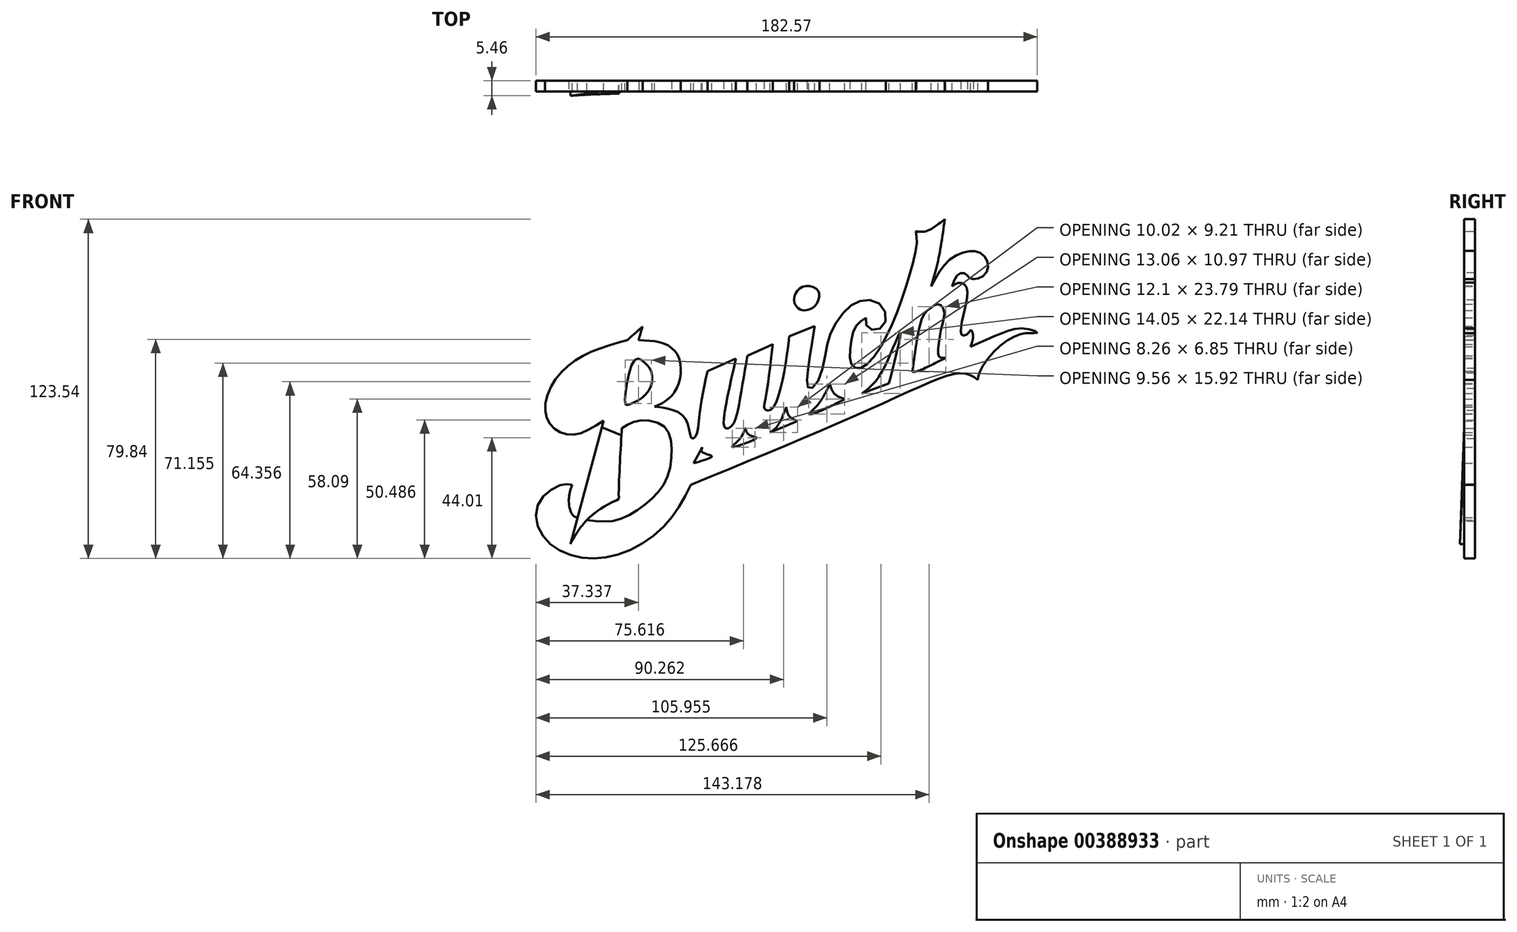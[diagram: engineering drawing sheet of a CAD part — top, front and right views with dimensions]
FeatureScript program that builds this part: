
annotation { "Feature Type Name" : "Feature", "Feature Type Description" : "" }
export const myFeature = defineFeature(function(context is Context, id is Id, definition is map)
    precondition{}
    {
        {
            var Q0;
            Q0=qCreatedBy(makeId("Front.planeOp"),FACE);
            var sketch = newSketch(context, id + "F0", { "sketchPlane" : qUnion([Q0])});
            skFitSpline(sketch, "E0", {"points": [v(-57.53, 21.82) * mm, v(-61.34, 4) * mm, v(-60.54, 3.6) * mm, v(-55.53, 5.8) * mm, v(-50.93, 11.4) * mm, v(-51.13, 17.81) * mm, v(-54.13, 21.22) * mm, v(-57.53, 21.82) * mm]});
            skFitSpline(sketch, "E1", {"points": [v(-62.74, -5.82) * mm, v(-63.94, -33.85) * mm, v(-63.94, -34.65) * mm, v(-65.54, -35.25) * mm, v(-75.96, -42.06) * mm, v(-83.57, -52.67) * mm], "startDerivative": vector(-6.03, -104.62) * mm, "endDerivative": vector(-25.26, -44.77) * mm});
            skFitSpline(sketch, "E2", {"points": [v(-83.57, -52.67) * mm, v(-70.15, -2.81) * mm], "startDerivative": vector(13.42, 49.86) * mm, "endDerivative": vector(13.42, 49.86) * mm});
            skFitSpline(sketch, "E3", {"points": [v(-70.15, -2.81) * mm, v(-81.96, -8.42) * mm, v(-90.17, -5.82) * mm, v(-93.78, 2) * mm, v(-88.97, 14.8) * mm, v(-76.56, 24.42) * mm, v(-60.54, 29.83) * mm], "startDerivative": vector(-70.6, -45.61) * mm, "endDerivative": vector(85.3, 23.4) * mm});
            skFitSpline(sketch, "E4", {"points": [v(-60.54, 29.83) * mm, v(-54.33, 35.23) * mm, v(-53.93, 35.43) * mm], "startDerivative": vector(9.9, 8.94) * mm, "endDerivative": vector(1.6, 0.53) * mm});
            skFitSpline(sketch, "E5", {"points": [v(-54.33, 35.23) * mm, v(-55.86, 29.83) * mm, v(-55.76, 29.83) * mm], "startDerivative": vector(-2.88, -8.83) * mm, "endDerivative": vector(1, 0.36) * mm});
            skFitSpline(sketch, "E6", {"points": [v(-55.76, 29.83) * mm, v(-45.65, 28.41) * mm, v(-39.84, 23.1) * mm, v(-39.44, 13.4) * mm, v(-43.55, 6.39) * mm, v(-49.46, 2.88) * mm], "startDerivative": vector(49.04, -1.87) * mm, "endDerivative": vector(-34.87, -16.17) * mm});
            skFitSpline(sketch, "E7", {"points": [v(-49.46, 2.88) * mm, v(-42.85, 1.78) * mm, v(-36.54, -2.81) * mm, v(-34.54, -9.83) * mm, v(-33.04, -9.43) * mm, v(-31.13, 1.08) * mm, v(-28.13, 17.3) * mm], "startDerivative": vector(41.75, -4.03) * mm, "endDerivative": vector(14.55, 66.04) * mm});
            skFitSpline(sketch, "E8", {"points": [v(-28.13, 17.3) * mm, v(-16.62, 22.3) * mm], "startDerivative": vector(11.51, 5) * mm, "endDerivative": vector(11.51, 5) * mm});
            skFitSpline(sketch, "E9", {"points": [v(-16.62, 22.3) * mm, v(-21.42, -1.72) * mm, v(-20.82, -5.82) * mm, v(-18.12, -4.73) * mm, v(-14.81, 6.89) * mm, v(-11.91, 23.5) * mm], "startDerivative": vector(-21.04, -92.35) * mm, "endDerivative": vector(11.83, 65.59) * mm});
            skFitSpline(sketch, "E10", {"points": [v(-11.91, 23.5) * mm, v(-1.7, 28.11) * mm], "startDerivative": vector(10.21, 4.6) * mm, "endDerivative": vector(10.21, 4.6) * mm});
            skFitSpline(sketch, "E11", {"points": [v(-1.7, 28.11) * mm, v(-4.8, 5.18) * mm, v(-5, 1.98) * mm, v(-2.9, 1.48) * mm, v(1, 8.49) * mm, v(4.4, 26.7) * mm, v(5, 31.32) * mm], "startDerivative": vector(-11.82, -100.44) * mm, "endDerivative": vector(3.65, 29.39) * mm});
            skFitSpline(sketch, "E12", {"points": [v(5, 31.32) * mm, v(15.22, 35.43) * mm], "startDerivative": vector(10.21, 4.12) * mm, "endDerivative": vector(10.21, 4.12) * mm});
            skFitSpline(sketch, "E13", {"points": [v(15.22, 35.43) * mm, v(12.72, 19.1) * mm, v(12.22, 11.8) * mm, v(13.12, 10.19) * mm, v(16.12, 12.5) * mm, v(19.53, 23.5) * mm, v(21.93, 33.02) * mm, v(28.14, 42.23) * mm, v(34.35, 45.83) * mm, v(41.25, 44.73) * mm, v(44.06, 38.32) * mm, v(40.65, 34.02) * mm, v(36.45, 35.23) * mm, v(35.95, 38.82) * mm], "startDerivative": vector(-23.4, -147.95) * mm, "endDerivative": vector(6.33, 71.21) * mm});
            skFitSpline(sketch, "E14", {"points": [v(35.95, 38.82) * mm, v(31.84, 35.23) * mm, v(29.64, 26.3) * mm, v(30.44, 19.6) * mm, v(34.14, 18.6) * mm, v(43.46, 29.83) * mm, v(52.16, 51.29) * mm, v(56.54, 69.03) * mm, v(56.2, 73.92) * mm], "startDerivative": vector(-49.1, -30.31) * mm, "endDerivative": vector(-8.6, 46.75) * mm});
            skFitSpline(sketch, "E15", {"points": [v(11.71, 51.77) * mm, v(7.88, 49.26) * mm, v(6.92, 45.73) * mm, v(8.99, 42.43) * mm, v(14.24, 42.7) * mm, v(17.08, 47.22) * mm, v(16.43, 50.07) * mm, v(11.71, 51.77) * mm]});
            skFitSpline(sketch, "E16", {"points": [v(56.2, 73.92) * mm, v(60.3, 73.92) * mm, v(67.89, 78.73) * mm], "startDerivative": vector(9.67, -1.63) * mm, "endDerivative": vector(13.46, 10.48) * mm});
            skFitSpline(sketch, "E17", {"points": [v(67.89, 78.73) * mm, v(65.21, 62.05) * mm, v(62.42, 51.62) * mm], "startDerivative": vector(-4.4, -31.84) * mm, "endDerivative": vector(-6.6, -22.02) * mm});
            skFitSpline(sketch, "E18", {"points": [v(62.42, 51.62) * mm, v(69.63, 62.14) * mm, v(78.36, 65.87) * mm, v(83.5, 64.2) * mm, v(85.34, 58.54) * mm, v(81.78, 54.88) * mm, v(78.07, 54.88) * mm, v(76.32, 56.72) * mm, v(73.68, 56.65) * mm, v(70.82, 51.62) * mm], "startDerivative": vector(37.14, 70.43) * mm, "endDerivative": vector(-21.1, -55.62) * mm});
            skFitSpline(sketch, "E19", {"points": [v(70.82, 51.62) * mm, v(73.7, 53.06) * mm, v(76.48, 51.62) * mm, v(76.47, 44.43) * mm, v(74.44, 35) * mm, v(74.99, 31.73) * mm, v(77.29, 32.47) * mm, v(78.42, 33.94) * mm, v(79.41, 31.94) * mm, v(78.27, 27.15) * mm], "startDerivative": vector(27.3, 20.2) * mm, "endDerivative": vector(-15.92, -39.23) * mm});
            skFitSpline(sketch, "E20", {"points": [v(78.27, 27.15) * mm, v(90.61, 32.55) * mm, v(100.18, 34.54) * mm, v(105.31, 32.88) * mm, v(102.97, 32.7) * mm, v(99.24, 32.4) * mm, v(89.8, 27.15) * mm, v(81.89, 16.65) * mm, v(81.3, 13.7) * mm], "startDerivative": vector(73.9, 33.44) * mm, "endDerivative": vector(-1.44, -30.66) * mm});
            skFitSpline(sketch, "E21", {"points": [v(81.3, 13.7) * mm, v(77.07, 16.13) * mm, v(69.34, 15.52) * mm, v(40.47, 3.16) * mm, v(-34.9, -28.77) * mm], "startDerivative": vector(-35.06, 26.28) * mm, "endDerivative": vector(-179.43, -74.24) * mm});
            skFitSpline(sketch, "E22", {"points": [v(-34.9, -28.77) * mm, v(-45.19, -45) * mm, v(-63.86, -56.83) * mm, v(-81.55, -57.64) * mm, v(-94.7, -49.38) * mm, v(-96.61, -36.52) * mm, v(-87.33, -28.77) * mm, v(-82.86, -28.77) * mm], "startDerivative": vector(-51.47, -102.54) * mm, "endDerivative": vector(49.25, -9.85) * mm});
            skFitSpline(sketch, "E23", {"points": [v(-82.86, -28.77) * mm, v(-84.16, -34.16) * mm, v(-82.86, -40.67) * mm, v(-80.69, -41.98) * mm], "startDerivative": vector(-4.96, -13.63) * mm, "endDerivative": vector(9.68, -2.98) * mm});
            skFitSpline(sketch, "E24", {"points": [v(-70.15, -2.81) * mm, v(-62.74, -5.82) * mm], "startDerivative": vector(7.4, -3) * mm, "endDerivative": vector(7.4, -3) * mm});
            skFitSpline(sketch, "E25", {"points": [v(-62.74, -5.82) * mm, v(-56.21, -2.81) * mm, v(-46.02, -4.82) * mm, v(-42.61, -13.6) * mm, v(-45, -27.07) * mm, v(-53.67, -36.87) * mm, v(-65.2, -43.11) * mm, v(-76.9, -43) * mm], "startDerivative": vector(49.94, 33) * mm, "endDerivative": vector(-80.48, 10.28) * mm});
            skFitSpline(sketch, "E26", {"points": [v(-33.77, -20) * mm, v(-30.2, -13.44) * mm], "startDerivative": vector(3.56, 6.56) * mm, "endDerivative": vector(3.56, 6.56) * mm});
            skFitSpline(sketch, "E27", {"points": [v(-30.2, -13.44) * mm, v(-30.2, -15.48) * mm, v(-26.41, -17.1) * mm, v(-33.77, -20) * mm], "startDerivative": vector(-3.88, -9.91) * mm, "endDerivative": vector(-26.18, -7.3) * mm});
            skFitSpline(sketch, "E28", {"points": [v(-18.12, -13.44) * mm, v(-14.84, -9.9) * mm, v(-12.77, -5.82) * mm, v(-11.46, -8.36) * mm, v(-8.31, -9.74) * mm, v(-18.12, -13.44) * mm]});
            skFitSpline(sketch, "E29", {"points": [v(-2.82, -7.55) * mm, v(0, -5.15) * mm, v(3.78, 2.68) * mm], "startDerivative": vector(7.32, 4.73) * mm, "endDerivative": vector(5.97, 15) * mm});
            skFitSpline(sketch, "E30", {"points": [v(3.78, 2.68) * mm, v(4.93, -0.84) * mm, v(8.31, -2.95) * mm], "startDerivative": vector(1.3, -7.9) * mm, "endDerivative": vector(7.73, -3.39) * mm});
            skFitSpline(sketch, "E31", {"points": [v(8.31, -2.95) * mm, v(-2.82, -7.55) * mm], "startDerivative": vector(-11.14, -4.6) * mm, "endDerivative": vector(-11.14, -4.6) * mm});
            skFitSpline(sketch, "E32", {"points": [v(12.93, 0) * mm, v(17.52, 4.98) * mm, v(21.33, 12.1) * mm], "startDerivative": vector(10.16, 9.65) * mm, "endDerivative": vector(6.69, 14.5) * mm});
            skFitSpline(sketch, "E33", {"points": [v(21.33, 12.1) * mm, v(23.4, 8) * mm, v(27.44, 5.93) * mm], "startDerivative": vector(3.1, -9.22) * mm, "endDerivative": vector(9.12, -3.13) * mm});
            skFitSpline(sketch, "E34", {"points": [v(27.44, 5.93) * mm, v(14.31, 0) * mm, v(12.93, 0) * mm], "startDerivative": vector(-21.53, -10.73) * mm, "endDerivative": vector(-4.5, 0.92) * mm});
            skFitSpline(sketch, "E35", {"points": [v(34.28, 8.23) * mm, v(40.47, 13.93) * mm, v(47.2, 27.22) * mm, v(49.8, 32.82) * mm, v(49.98, 32.42) * mm, v(45.54, 13.26) * mm, v(45.3, 12.1) * mm], "startDerivative": vector(33.83, 24.66) * mm, "endDerivative": vector(-0.88, -7.69) * mm});
            skFitSpline(sketch, "E36", {"points": [v(45.33, 12.29) * mm, v(34.28, 8.23) * mm], "startDerivative": vector(-11.05, -4.06) * mm, "endDerivative": vector(-11.05, -4.06) * mm});
            skFitSpline(sketch, "E37", {"points": [v(54.82, 17.04) * mm, v(59.37, 40.07) * mm, v(62.2, 42.78) * mm, v(65.27, 44.4) * mm, v(67.57, 41.69) * mm, v(66.8, 35.82) * mm, v(65.2, 26.15) * mm, v(65.73, 23.01) * mm, v(68.26, 22.66) * mm], "startDerivative": vector(15.2, 117.36) * mm, "endDerivative": vector(36.44, 1.7) * mm});
            skFitSpline(sketch, "E38", {"points": [v(54.82, 17.04) * mm, v(56.1, 17.04) * mm, v(68.26, 22.66) * mm], "startDerivative": vector(4.17, -0.87) * mm, "endDerivative": vector(19.93, 10.17) * mm});
            skLineSegment(sketch, "E39", {"start": v(45.33, 12.29) * mm, "end": v(45.33, 12.29) * mm});
            skSolve(sketch);
        }
        {
            var Q0;
            Q0=makeQuery(id+"F0.imprint","IMPRINT",FACE,{"disambiguationData":[TD([[makeQuery(id+"F0.imprint","IMPRINT",EDGE,{"derivedFrom":sQuery(id+"F0.wireOp",EDGE,"E0")}),-1.0]])]});
            var Q1;
            Q1=makeQuery(id+"F0.imprint","IMPRINT",FACE,{"disambiguationData":[TD([[makeQuery(id+"F0.imprint","IMPRINT",EDGE,{"derivedFrom":sQuery(id+"F0.wireOp",EDGE,"E15")}),1.0]])]});
            extrude(context, id + "F1", {"entities" : qUnion([Q0, Q1]), "depth" : 4.3 * mm});
        }
        {
            var Q0;
            {var subQ0=sQuery(id+"F0.wireOp",EDGE,"E24");Q0=makeQuery(id+"F0.imprint","IMPRINT",FACE,{"disambiguationData":[TD([[makeQuery(id+"F0.imprint","IMPRINT",EDGE,{"derivedFrom":subQ0}),-1.0]])]});}
            extrude(context, id + "F2", {"entities" : qUnion([Q0]), "operationType" : NewBodyOperationType.ADD, "depth" : 6.2 * mm});
        }
        {
            var Q0;
            Q0=makeQuery(id+"F2.opExtrude","CAP_EDGE",EDGE,{"disambiguationData":[OSD([sQuery(id+"F0.wireOp",EDGE,"E24")])],"isStart":false});
            chamfer(context, id + "F3", {"entities" : qUnion([Q0]), "chamferType" : ChamferType.TWO_OFFSETS, "width1" : 2 * mm, "oppositeDirection" : false, "width2" : 55 * mm, "tangentPropagation" : true});
        }
        {
            var Q0;
            Q0=makeQuery(id+"F1.opExtrude","SWEPT_BODY",BODY,{"disambiguationData":[OSD([sQuery(id+"F0.wireOp",EDGE,"E0"),sQuery(id+"F0.wireOp",EDGE,"E1"),sQuery(id+"F0.wireOp",EDGE,"E2"),sQuery(id+"F0.wireOp",EDGE,"E3"),sQuery(id+"F0.wireOp",EDGE,"E4"),sQuery(id+"F0.wireOp",EDGE,"E5"),sQuery(id+"F0.wireOp",EDGE,"E6"),sQuery(id+"F0.wireOp",EDGE,"E7"),sQuery(id+"F0.wireOp",EDGE,"E8"),sQuery(id+"F0.wireOp",EDGE,"E9"),sQuery(id+"F0.wireOp",EDGE,"E10"),sQuery(id+"F0.wireOp",EDGE,"E11"),sQuery(id+"F0.wireOp",EDGE,"E12"),sQuery(id+"F0.wireOp",EDGE,"E13"),sQuery(id+"F0.wireOp",EDGE,"E14"),sQuery(id+"F0.wireOp",EDGE,"E16"),sQuery(id+"F0.wireOp",EDGE,"E17"),sQuery(id+"F0.wireOp",EDGE,"E18"),sQuery(id+"F0.wireOp",EDGE,"E19"),sQuery(id+"F0.wireOp",EDGE,"E20"),sQuery(id+"F0.wireOp",EDGE,"E21"),sQuery(id+"F0.wireOp",EDGE,"E22"),sQuery(id+"F0.wireOp",EDGE,"E23"),sQuery(id+"F0.wireOp",EDGE,"E24"),sQuery(id+"F0.wireOp",EDGE,"E25"),sQuery(id+"F0.wireOp",EDGE,"E26"),sQuery(id+"F0.wireOp",EDGE,"E27"),sQuery(id+"F0.wireOp",EDGE,"E28"),sQuery(id+"F0.wireOp",EDGE,"E29"),sQuery(id+"F0.wireOp",EDGE,"E30"),sQuery(id+"F0.wireOp",EDGE,"E31"),sQuery(id+"F0.wireOp",EDGE,"E32"),sQuery(id+"F0.wireOp",EDGE,"E33"),sQuery(id+"F0.wireOp",EDGE,"E34"),sQuery(id+"F0.wireOp",EDGE,"E37"),sQuery(id+"F0.wireOp",EDGE,"E38")])]});
            var Q1;
            Q1=makeQuery(id+"F1.opExtrude","SWEPT_BODY",BODY,{"disambiguationData":[OSD([sQuery(id+"F0.wireOp",EDGE,"E15")])]});
            var Q2;
            Q2=qCreatedBy(makeId("Origin.pointOp"),VERTEX);
            transform(context, id + "F4", {"entities" : qUnion([Q0, Q1]), "transformType" : TransformType.SCALE_UNIFORMLY, "scale" : 0.9, "scalePoint" : qUnion([Q2]), "makeCopy" : false});
        }
    });
